# Revit family: Domino 2ER 30
name_source: partatom
category: Equipamento especial
revit_build: Autodesk Revit 2016 (Build: 20150220_1215(x64)
units: mm (PartAtom-declared; Revit-internal decimal feet)

## family parameters
Com base no plano de trabalho = Não
Compartilhado = Não
Corte com vazios quando carregados = Não
Cota do conector redondo = Utilizar diâmetro
Ponto de cálculo do ambiente = Não
Sempre na vertical = Sim
Tipo de parte = Normal

## types (1)
- Domino ER
    Classe de Construção = Classe 1
    Consumo máximo = 3,0 kWh
    Código de montagem = 94700/310
    Descrição = Tramontina Cooktop Elétrico
    Desenvolvedor = Factory Cursos & Desenvolvimento
    Disjuntor termomagnético = 16 A
    Domino 2ER 30 = 0  [stored 0 ft]
    Fabricante = Tramontina
    Frequência = 50 - 60 Hz
    Grau de Proteção = IPX0
    Modelo = Tramontina - Dominó 2ER 30
    Peso Bruto = 6,4 kg
    Peso liquido = 5,4 kg
    Potência das áreas de aquecimento - 180 mm Diametro = 1,7 kW (2x)
    Potência máxima = 3,0 kW
    Potência áreas de aquecimento - 145 mm Diametro = 1,3 kW
    Site do desenvolvedor = www.factorycursos.com.br
    Tensão = 220 V
    Tipo de imagem = 94700 310.jpg
    Tramontina = Tramontina
    URL = www.tramontina.com.br

note: [stored X ft] marks values corroborated as IEEE doubles in the binary element streams (Revit-internal decimal feet)
